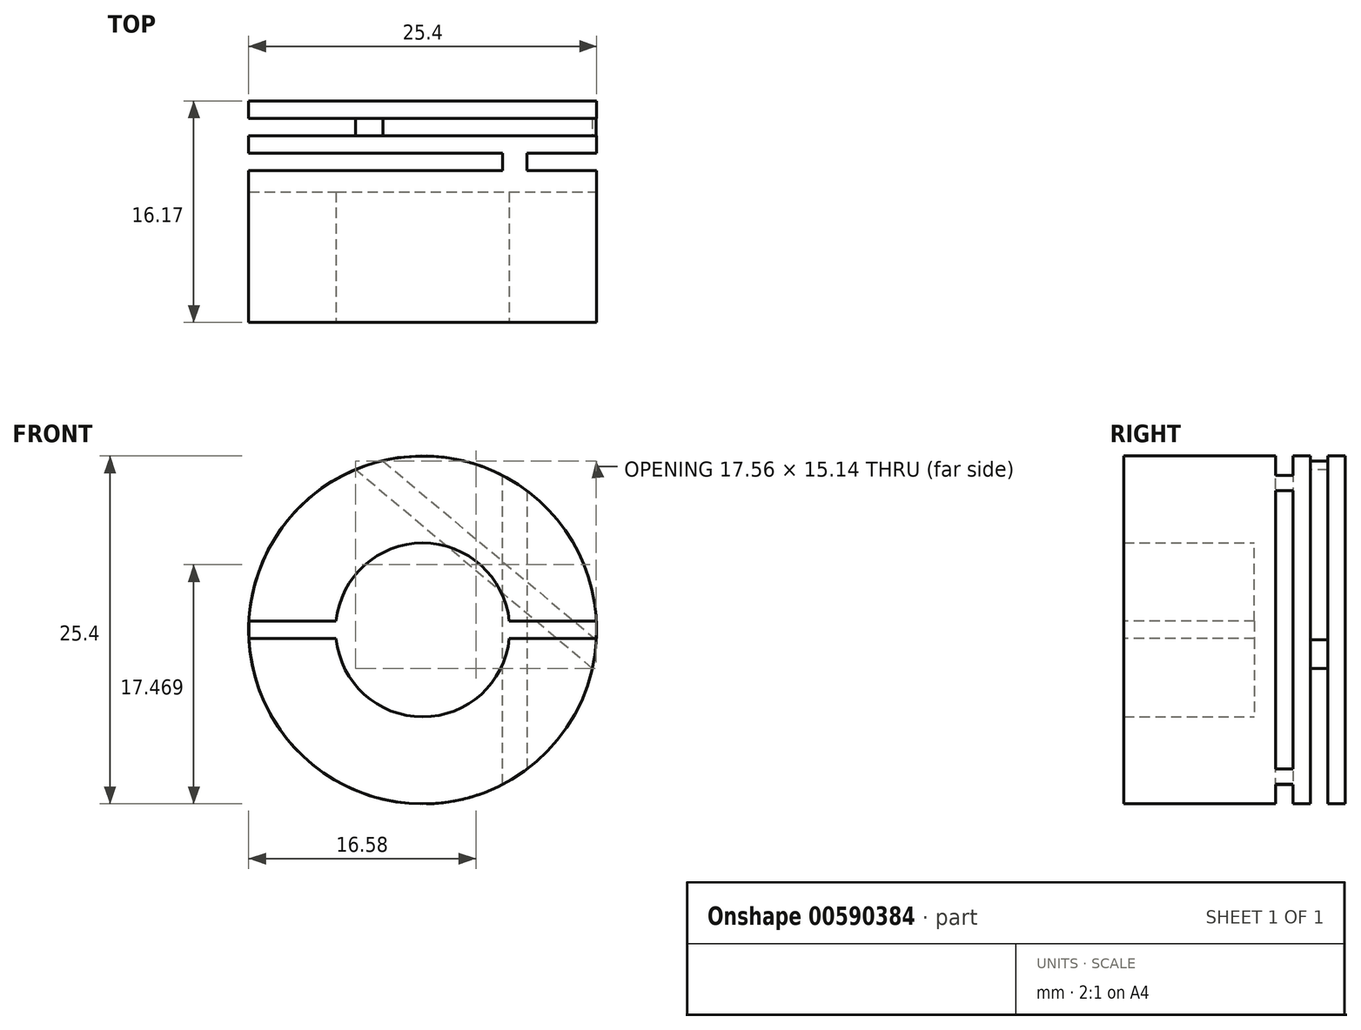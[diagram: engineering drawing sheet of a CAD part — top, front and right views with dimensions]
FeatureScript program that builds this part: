
annotation { "Feature Type Name" : "Feature", "Feature Type Description" : "" }
export const myFeature = defineFeature(function(context is Context, id is Id, definition is map)
    precondition{}
    {
        {
            var Q0;
            Q0=qCreatedBy(makeId("Front.planeOp"),FACE);
            var sketch = newSketch(context, id + "F0", { "sketchPlane" : qUnion([Q0])});
            skCircle(sketch, "E0", {"center": v(0, 0) * mm, "radius": 12.7 * mm});
            skCircle(sketch, "E1", {"center": v(0, 0) * mm, "radius": 6.35 * mm});
            skSolve(sketch);
        }
        {
            var Q0;
            Q0=makeQuery(id+"F0.imprint","IMPRINT",FACE,{"disambiguationData":[TD([[makeQuery(id+"F0.imprint","IMPRINT",EDGE,{"derivedFrom":sQuery(id+"F0.wireOp",EDGE,"E0")}),1.0]])]});
            extrude(context, id + "F1", {"entities" : qUnion([Q0]), "depth" : 9.52 * mm, "offsetDistance" : 25.4 * mm});
        }
        {
            var Q0;
            Q0=makeQuery(id+"F1.opExtrude","CAP_FACE",FACE,{"disambiguationData":[OSD([sQuery(id+"F0.wireOp",EDGE,"E0"),sQuery(id+"F0.wireOp",EDGE,"E1")])],"isStart":false});
            var sketch = newSketch(context, id + "F2", { "sketchPlane" : qUnion([Q0])});
            skLineSegment(sketch, "E2", {"start": v(6.32, 0.63) * mm, "end": v(12.67, 0.63) * mm});
            skLineSegment(sketch, "E3", {"start": v(6.31, -0.64) * mm, "end": v(12.67, -0.64) * mm});
            skLineSegment(sketch, "E4", {"start": v(12.67, -0.64) * mm, "end": v(12.67, -0.64) * mm});
            skLineSegment(sketch, "E5", {"start": v(-12.67, 0.64) * mm, "end": v(-6.31, 0.64) * mm});
            skLineSegment(sketch, "E6", {"start": v(-12.67, -0.64) * mm, "end": v(-6.31, -0.64) * mm});
            skLineSegment(sketch, "E7.left", {"start": v(-12.67, 0.63) * mm, "end": v(-12.67, -0.64) * mm});
            skLineSegment(sketch, "E7.right", {"start": v(-6.31, 0.64) * mm, "end": v(-6.31, -0.64) * mm});
            skLineSegment(sketch, "E8.top", {"start": v(6.32, -0.64) * mm, "end": v(12.67, -0.64) * mm});
            skLineSegment(sketch, "E8.left", {"start": v(6.32, 0.63) * mm, "end": v(6.32, -0.64) * mm});
            skLineSegment(sketch, "E8.right", {"start": v(12.67, 0.63) * mm, "end": v(12.67, -0.64) * mm});
            skSolve(sketch);
        }
        {
            var Q0;
            {var subQ2=sQuery(id+"F0.wireOp",EDGE,"E0");var subQ6=sQuery(id+"F0.wireOp",EDGE,"E1");Q0=makeQuery(id+"F7.boolean.opBoolean","SPLIT",FACE,{"disambiguationData":[TD([makeQuery(id+"F1.opExtrude","SWEPT_FACE",FACE,{"disambiguationData":[OSD([subQ6])]})])],"derivedFrom":makeQuery(id+"F1.opExtrude","CAP_FACE",FACE,{"disambiguationData":[OSD([subQ2,subQ6])],"isStart":true})});}
            var sketch = newSketch(context, id + "F3", { "sketchPlane" : qUnion([Q0])});
            skCircle(sketch, "E9", {"center": v(0, 0) * mm, "radius": 12.7 * mm});
            skSolve(sketch);
        }
        {
            var Q0;
            Q0=makeQuery(id+"F3.imprint","IMPRINT",FACE,{"disambiguationData":[TD([[makeQuery(id+"F3.imprint","IMPRINT",EDGE,{"derivedFrom":makeQuery(id+"F1.opExtrude","CAP_EDGE",EDGE,{"disambiguationData":[OSD([sQuery(id+"F0.wireOp",EDGE,"E1")])],"isStart":true})}),-1.0]])]});
            var Q1;
            Q1=makeQuery(id+"F3.imprint","IMPRINT",FACE,{"disambiguationData":[TD([[makeQuery(id+"F3.imprint","IMPRINT",EDGE,{"derivedFrom":sQuery(id+"F3.wireOp",EDGE,"E9")}),-1.0]])]});
            extrude(context, id + "F4", {"entities" : qUnion([Q0, Q1]), "operationType" : NewBodyOperationType.ADD, "depth" : 1.56 * mm, "offsetDistance" : 25.4 * mm});
        }
        {
            var Q0;
            {var subQ0=sQuery(id+"F2.wireOp",EDGE,"E7.left");Q0=makeQuery(id+"F2.imprint","IMPRINT",FACE,{"disambiguationData":[TD([[makeQuery(id+"F2.imprint","IMPRINT",EDGE,{"derivedFrom":subQ0}),1.0]])]});}
            var Q1;
            {var subQ0=sQuery(id+"F2.wireOp",EDGE,"E8.right");Q1=makeQuery(id+"F2.imprint","IMPRINT",FACE,{"disambiguationData":[TD([[makeQuery(id+"F2.imprint","IMPRINT",EDGE,{"derivedFrom":subQ0}),-1.0]])]});}
            extrude(context, id + "F5", {"entities" : qUnion([Q0, Q1]), "operationType" : NewBodyOperationType.REMOVE, "depth" : -9.52 * mm, "offsetDistance" : 25.4 * mm});
        }
        {
            var Q0;
            Q0=makeQuery(id+"F4.opExtrude","CAP_FACE",FACE,{"disambiguationData":[OSD([sQuery(id+"F3.wireOp",EDGE,"E9")])],"isStart":false});
            var sketch = newSketch(context, id + "F6", { "sketchPlane" : qUnion([Q0])});
            skLineSegment(sketch, "E10", {"start": v(-5.84, -11.28) * mm, "end": v(-5.84, 11.27) * mm});
            skPoint(sketch, "E11.orphan", {"position": v(-12.7, 0) * mm});
            skLineSegment(sketch, "E12", {"start": v(-7.62, 10.16) * mm, "end": v(-7.62, -10.16) * mm});
            skArc(sketch, "E13", {"start": v(-5.84, 11.27) * mm, "mid": v(-6.76, 10.76) * mm, "end": v(-7.62, 10.16) * mm});
            skArc(sketch, "E14", {"start": v(-7.62, -10.16) * mm, "mid": v(-6.76, -10.76) * mm, "end": v(-5.84, -11.28) * mm});
            skSolve(sketch);
        }
        {
            var Q0;
            {var subQ5=sQuery(id+"F6.wireOp",EDGE,"E12");Q0=makeQuery(id+"F6.imprint","IMPRINT",FACE,{"disambiguationData":[TD([[makeQuery(id+"F6.imprint","IMPRINT",EDGE,{"derivedFrom":subQ5}),1.0]])]});}
            extrude(context, id + "F7", {"entities" : qUnion([Q0]), "operationType" : NewBodyOperationType.ADD, "depth" : 1.27 * mm, "offsetDistance" : 25.4 * mm});
        }
        {
            var Q0;
            Q0=makeQuery(id+"F7.opExtrude","CAP_FACE",FACE,{"disambiguationData":[OSD([sQuery(id+"F3.wireOp",EDGE,"E9"),sQuery(id+"F6.wireOp",EDGE,"E10"),sQuery(id+"F6.wireOp",EDGE,"E12"),sQuery(id+"F6.wireOp",EDGE,"E13"),sQuery(id+"F6.wireOp",EDGE,"E14")])],"isStart":false});
            var sketch = newSketch(context, id + "F8", { "sketchPlane" : qUnion([Q0])});
            skCircle(sketch, "E15", {"center": v(0, 0) * mm, "radius": 12.7 * mm});
            skSolve(sketch);
        }
        {
            var Q0;
            Q0 = qSketchRegion(id + "F8", true);
            extrude(context, id + "F9", {"entities" : qUnion([Q0]), "operationType" : NewBodyOperationType.ADD, "depth" : 1.27 * mm, "offsetDistance" : 25.4 * mm});
        }
        {
            var Q0;
            Q0=makeQuery(id+"F9.opExtrude","CAP_FACE",FACE,{"disambiguationData":[OSD([sQuery(id+"F8.wireOp",EDGE,"E15")])],"isStart":false});
            var sketch = newSketch(context, id + "F10", { "sketchPlane" : qUnion([Q0])});
            skLineSegment(sketch, "E16", {"start": v(-12.37, -2.8) * mm, "end": v(4.9, 11.7) * mm});
            skPoint(sketch, "E17.orphan", {"position": v(-4.75, 0.02) * mm});
            skLineSegment(sketch, "E18", {"start": v(2.9, 12.34) * mm, "end": v(-12.66, -0.72) * mm});
            skArc(sketch, "E19", {"start": v(4.9, 11.7) * mm, "mid": v(3.92, 12.06) * mm, "end": v(2.9, 12.34) * mm});
            skArc(sketch, "E20", {"start": v(-12.66, -0.72) * mm, "mid": v(-12.57, -1.77) * mm, "end": v(-12.37, -2.8) * mm});
            skSolve(sketch);
        }
        {
            var Q0;
            Q0=makeQuery(id+"F10.imprint","IMPRINT",FACE,{"disambiguationData":[TD([[makeQuery(id+"F10.imprint","IMPRINT",EDGE,{"derivedFrom":sQuery(id+"F10.wireOp",EDGE,"E16")}),1.0]])]});
            extrude(context, id + "F11", {"entities" : qUnion([Q0]), "operationType" : NewBodyOperationType.ADD, "depth" : 1.27 * mm, "offsetDistance" : 25.4 * mm});
        }
        {
            var Q0;
            Q0=makeQuery(id+"F11.opExtrude","CAP_FACE",FACE,{"disambiguationData":[OSD([sQuery(id+"F10.wireOp",EDGE,"E16"),sQuery(id+"F10.wireOp",EDGE,"E18"),sQuery(id+"F10.wireOp",EDGE,"E19"),sQuery(id+"F10.wireOp",EDGE,"E20")])],"isStart":false});
            var sketch = newSketch(context, id + "F12", { "sketchPlane" : qUnion([Q0])});
            skCircle(sketch, "E21", {"center": v(0, 0) * mm, "radius": 12.7 * mm});
            skSolve(sketch);
        }
        {
            var Q0;
            {var subQ5=makeQuery(id+"F11.opExtrude","CAP_EDGE",EDGE,{"disambiguationData":[OSD([sQuery(id+"F10.wireOp",EDGE,"E19")])],"isStart":false});Q0=makeQuery(id+"F12.imprint","IMPRINT",FACE,{"disambiguationData":[TD([[makeQuery(id+"F12.imprint","IMPRINT",EDGE,{"derivedFrom":subQ5}),-1.0]])]});}
            var Q1;
            Q1=makeQuery(id+"F12.imprint","IMPRINT",FACE,{"disambiguationData":[TD([[makeQuery(id+"F12.imprint","IMPRINT",EDGE,{"derivedFrom":makeQuery(id+"F11.opExtrude","CAP_EDGE",EDGE,{"disambiguationData":[OSD([sQuery(id+"F10.wireOp",EDGE,"E16")])],"isStart":false})}),1.0]])]});
            extrude(context, id + "F13", {"entities" : qUnion([Q0, Q1]), "operationType" : NewBodyOperationType.ADD, "depth" : 1.27 * mm, "offsetDistance" : 25.4 * mm});
        }
    });
